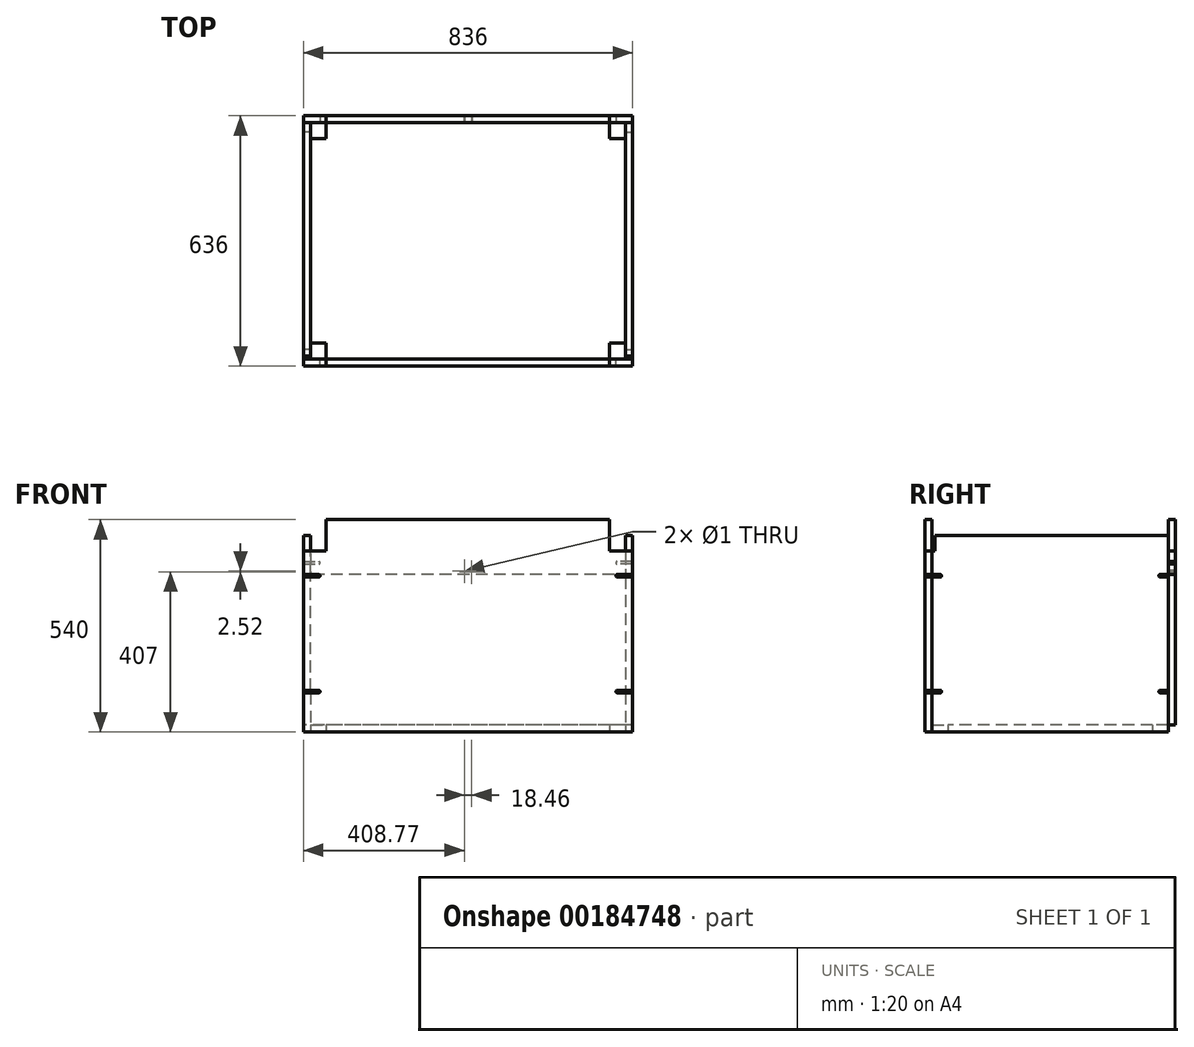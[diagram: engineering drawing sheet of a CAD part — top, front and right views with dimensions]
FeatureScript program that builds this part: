
annotation { "Feature Type Name" : "Feature", "Feature Type Description" : "" }
export const myFeature = defineFeature(function(context is Context, id is Id, definition is map)
    precondition{}
    {
        {
            var Q0;
            Q0=qCreatedBy(makeId("Front.planeOp"),FACE);
            var sketch = newSketch(context, id + "F0", { "sketchPlane" : qUnion([Q0])});
            skLineSegment(sketch, "E0.bottom", {"start": v(418, -250) * mm, "end": v(-418, -250) * mm});
            skLineSegment(sketch, "E0.top", {"start": v(418, 250) * mm, "end": v(-418, 250) * mm});
            skLineSegment(sketch, "E0.left", {"start": v(418, -250) * mm, "end": v(418, 250) * mm});
            skLineSegment(sketch, "E0.right", {"start": v(-418, -250) * mm, "end": v(-418, 250) * mm});
            skPoint(sketch, "E0.middle", {"position": v(0, 0) * mm});
            skLineSegment(sketch, "E1.bottom", {"start": v(-418, 150) * mm, "end": v(-378.8, 150) * mm});
            skLineSegment(sketch, "E1.top", {"start": v(-418, 144) * mm, "end": v(-378.8, 144) * mm});
            skLineSegment(sketch, "E1.left", {"start": v(-418, 150) * mm, "end": v(-418, 144) * mm});
            skLineSegment(sketch, "E1.right", {"start": v(-378.8, 150) * mm, "end": v(-378.8, 144) * mm, "construction": true});
            skArc(sketch, "E2", {"start": v(-378.8, 144) * mm, "mid": v(-375.8, 147) * mm, "end": v(-378.8, 150) * mm});
            skLineSegment(sketch, "E3.MirrorCS", {"start": v(418, 150) * mm, "end": v(378.8, 150) * mm});
            skLineSegment(sketch, "E4.MirrorCS", {"start": v(418, 144) * mm, "end": v(378.8, 144) * mm});
            skArc(sketch, "E5.MirrorCS", {"start": v(378.8, 144) * mm, "mid": v(375.8, 147) * mm, "end": v(378.8, 150) * mm});
            skLineSegment(sketch, "E6.MirrorCS", {"start": v(418, 150) * mm, "end": v(418, 144) * mm});
            skLineSegment(sketch, "E7.MirrorCS", {"start": v(-418, -150) * mm, "end": v(-378.8, -150) * mm});
            skArc(sketch, "E8.MirrorCS", {"start": v(-378.8, -144) * mm, "mid": v(-375.8, -147) * mm, "end": v(-378.8, -150) * mm});
            skLineSegment(sketch, "E9.MirrorCS", {"start": v(-418, -144) * mm, "end": v(-378.8, -144) * mm});
            skLineSegment(sketch, "E10.MirrorCS", {"start": v(-418, -150) * mm, "end": v(-418, -144) * mm});
            skLineSegment(sketch, "E11.MirrorCS", {"start": v(418, -150) * mm, "end": v(378.8, -150) * mm});
            skLineSegment(sketch, "E12.MirrorCS", {"start": v(418, -144) * mm, "end": v(378.8, -144) * mm});
            skArc(sketch, "E13.MirrorCS", {"start": v(378.8, -144) * mm, "mid": v(375.8, -147) * mm, "end": v(378.8, -150) * mm});
            skLineSegment(sketch, "E14.MirrorCS", {"start": v(418, -150) * mm, "end": v(418, -144) * mm});
            skSolve(sketch);
        }
        {
            var Q0;
            Q0=makeQuery(id+"F0.imprint","IMPRINT",FACE,{"disambiguationData":[TD([[makeQuery(id+"F0.imprint","IMPRINT",EDGE,{"derivedFrom":sQuery(id+"F0.wireOp",EDGE,"E0.bottom")}),-1.0]])]});
            extrude(context, id + "F1", {"entities" : qUnion([Q0]), "depth" : 18 * mm});
        }
        {
            var Q0;
            Q0=makeQuery(id+"F1.opExtrude","SWEPT_FACE",FACE,{"disambiguationData":[OSD([sQuery(id+"F0.wireOp",EDGE,"E0.left")])]});
            var sketch = newSketch(context, id + "F2", { "sketchPlane" : qUnion([Q0])});
            skLineSegment(sketch, "E15.bottom", {"start": v(0, 250) * mm, "end": v(600, 250) * mm});
            skLineSegment(sketch, "E15.top", {"start": v(0, -250) * mm, "end": v(600, -250) * mm});
            skLineSegment(sketch, "E15.left", {"start": v(0, 250) * mm, "end": v(0, -250) * mm});
            skLineSegment(sketch, "E15.right", {"start": v(600, 250) * mm, "end": v(600, -250) * mm});
            skLineSegment(sketch, "E16.bottom", {"start": v(0, 150) * mm, "end": v(21.2, 150) * mm});
            skLineSegment(sketch, "E16.top", {"start": v(0, 144) * mm, "end": v(21.2, 144) * mm});
            skLineSegment(sketch, "E16.left", {"start": v(0, 150) * mm, "end": v(0, 144) * mm});
            skLineSegment(sketch, "E16.right", {"start": v(21.2, 150) * mm, "end": v(21.2, 144) * mm, "construction": true});
            skArc(sketch, "E17", {"start": v(21.2, 144) * mm, "mid": v(24.2, 147) * mm, "end": v(21.2, 150) * mm});
            skLineSegment(sketch, "E18.MirrorCS", {"start": v(0, -150) * mm, "end": v(21.2, -150) * mm});
            skLineSegment(sketch, "E19.MirrorCS", {"start": v(0, -144) * mm, "end": v(21.2, -144) * mm});
            skArc(sketch, "E20.MirrorCS", {"start": v(21.2, -144) * mm, "mid": v(24.2, -147) * mm, "end": v(21.2, -150) * mm});
            skLineSegment(sketch, "E21.MirrorCS", {"start": v(0, -150) * mm, "end": v(0, -144) * mm});
            skLineSegment(sketch, "E22", {"start": v(300, 250) * mm, "end": v(300, 116.64) * mm, "construction": true});
            skLineSegment(sketch, "E23.MirrorCS", {"start": v(600, 150) * mm, "end": v(578.8, 150) * mm});
            skLineSegment(sketch, "E24.MirrorCS", {"start": v(600, 144) * mm, "end": v(578.8, 144) * mm});
            skArc(sketch, "E25.MirrorCS", {"start": v(578.8, 144) * mm, "mid": v(575.8, 147) * mm, "end": v(578.8, 150) * mm});
            skLineSegment(sketch, "E26.MirrorCS", {"start": v(600, 150) * mm, "end": v(600, 144) * mm});
            skLineSegment(sketch, "E27.MirrorCS", {"start": v(600, -144) * mm, "end": v(578.8, -144) * mm});
            skLineSegment(sketch, "E28.MirrorCS", {"start": v(600, -150) * mm, "end": v(578.8, -150) * mm});
            skArc(sketch, "E29.MirrorCS", {"start": v(578.8, -144) * mm, "mid": v(575.8, -147) * mm, "end": v(578.8, -150) * mm});
            skSolve(sketch);
        }
        {
            var Q0;
            Q0=makeQuery(id+"F2.imprint","IMPRINT",FACE,{"disambiguationData":[TD([[makeQuery(id+"F2.imprint","IMPRINT",EDGE,{"derivedFrom":sQuery(id+"F2.wireOp",EDGE,"E15.bottom")}),-1.0]])]});
            extrude(context, id + "F3", {"entities" : qUnion([Q0]), "oppositeDirection" : true, "depth" : 18 * mm});
        }
        {
            var Q0;
            {var subQ0=sQuery(id+"F0.wireOp",EDGE,"E0.right");Q0=makeQuery(id+"F1.opExtrude","SWEPT_FACE",FACE,{"disambiguationData":[OSD([subQ0]),TDD([makeQuery(id+"F0.imprint","IMPRINT",EDGE,{"disambiguationData":[TD([[makeQuery(id+"F0.imprint","INTERSECT",VERTEX,{"derivedFrom":[subQ0,sQuery(id+"F0.wireOp",EDGE,"E1.top"),sQuery(id+"F0.wireOp",EDGE,"E1.left")]}),1.0]])],"derivedFrom":subQ0})])]});}
            var sketch = newSketch(context, id + "F4", { "sketchPlane" : qUnion([Q0])});
            skLineSegment(sketch, "E30.0.0", {"start": v(0, 250) * mm, "end": v(-600, 250) * mm});
            skLineSegment(sketch, "E30.0.1", {"start": v(-600, 250) * mm, "end": v(-600, 150) * mm});
            skLineSegment(sketch, "E30.0.2", {"start": v(-600, 150) * mm, "end": v(-578.8, 150) * mm});
            skArc(sketch, "E30.0.3", {"start": v(-578.8, 150) * mm, "mid": v(-575.8, 147) * mm, "end": v(-578.8, 144) * mm});
            skLineSegment(sketch, "E30.0.4", {"start": v(-578.8, 144) * mm, "end": v(-600, 144) * mm});
            skLineSegment(sketch, "E30.0.5", {"start": v(-600, 144) * mm, "end": v(-600, -144) * mm});
            skLineSegment(sketch, "E30.0.6", {"start": v(-600, -144) * mm, "end": v(-578.8, -144) * mm});
            skArc(sketch, "E30.0.7", {"start": v(-578.8, -144) * mm, "mid": v(-575.8, -147) * mm, "end": v(-578.8, -150) * mm});
            skLineSegment(sketch, "E30.0.8", {"start": v(-578.8, -150) * mm, "end": v(-600, -150) * mm});
            skLineSegment(sketch, "E30.0.9", {"start": v(-600, -150) * mm, "end": v(-600, -250) * mm});
            skLineSegment(sketch, "E30.0.10", {"start": v(-600, -250) * mm, "end": v(0, -250) * mm});
            skLineSegment(sketch, "E30.0.11", {"start": v(0, -250) * mm, "end": v(0, -150) * mm});
            skLineSegment(sketch, "E30.0.12", {"start": v(0, -150) * mm, "end": v(-21.2, -150) * mm});
            skArc(sketch, "E30.0.13", {"start": v(-21.2, -150) * mm, "mid": v(-24.2, -147) * mm, "end": v(-21.2, -144) * mm});
            skLineSegment(sketch, "E30.0.14", {"start": v(-21.2, -144) * mm, "end": v(0, -144) * mm});
            skLineSegment(sketch, "E30.0.15", {"start": v(0, -144) * mm, "end": v(0, 144) * mm});
            skLineSegment(sketch, "E30.0.16", {"start": v(0, 144) * mm, "end": v(-21.2, 144) * mm});
            skArc(sketch, "E30.0.17", {"start": v(-21.2, 144) * mm, "mid": v(-24.2, 147) * mm, "end": v(-21.2, 150) * mm});
            skLineSegment(sketch, "E30.0.18", {"start": v(-21.2, 150) * mm, "end": v(0, 150) * mm});
            skLineSegment(sketch, "E30.0.19", {"start": v(0, 150) * mm, "end": v(0, 250) * mm});
            skSolve(sketch);
        }
        {
            var Q0;
            Q0=makeQuery(id+"F4.imprint","IMPRINT",FACE,{"disambiguationData":[TD([[makeQuery(id+"F4.imprint","IMPRINT",EDGE,{"derivedFrom":sQuery(id+"F4.wireOp",EDGE,"E30.0.0")}),1.0]])]});
            extrude(context, id + "F5", {"entities" : qUnion([Q0]), "oppositeDirection" : true, "depth" : 18 * mm});
        }
        {
            var Q0;
            Q0=makeQuery(id+"F1.opExtrude","CAP_FACE",FACE,{"disambiguationData":[OSD([sQuery(id+"F0.wireOp",EDGE,"E0.bottom"),sQuery(id+"F0.wireOp",EDGE,"E0.top"),sQuery(id+"F0.wireOp",EDGE,"E0.left"),sQuery(id+"F0.wireOp",EDGE,"E0.right"),sQuery(id+"F0.wireOp",EDGE,"E1.bottom"),sQuery(id+"F0.wireOp",EDGE,"E1.top"),sQuery(id+"F0.wireOp",EDGE,"E2"),sQuery(id+"F0.wireOp",EDGE,"E3.MirrorCS"),sQuery(id+"F0.wireOp",EDGE,"E4.MirrorCS"),sQuery(id+"F0.wireOp",EDGE,"E5.MirrorCS"),sQuery(id+"F0.wireOp",EDGE,"E7.MirrorCS"),sQuery(id+"F0.wireOp",EDGE,"E8.MirrorCS"),sQuery(id+"F0.wireOp",EDGE,"E9.MirrorCS"),sQuery(id+"F0.wireOp",EDGE,"E11.MirrorCS"),sQuery(id+"F0.wireOp",EDGE,"E12.MirrorCS"),sQuery(id+"F0.wireOp",EDGE,"E13.MirrorCS")])],"isStart":false});
            var sketch = newSketch(context, id + "F6", { "sketchPlane" : qUnion([Q0])});
            skLineSegment(sketch, "E31.bottom", {"start": v(-418, 250) * mm, "end": v(-360, 250) * mm});
            skLineSegment(sketch, "E31.top", {"start": v(-418, 210) * mm, "end": v(-360, 210) * mm});
            skLineSegment(sketch, "E31.left", {"start": v(-418, 250) * mm, "end": v(-418, 210) * mm});
            skLineSegment(sketch, "E31.right", {"start": v(-360, 250) * mm, "end": v(-360, 210) * mm});
            skLineSegment(sketch, "E32.MirrorCS", {"start": v(418, 210) * mm, "end": v(360, 210) * mm});
            skLineSegment(sketch, "E33.MirrorCS", {"start": v(418, 250) * mm, "end": v(418, 210) * mm});
            skLineSegment(sketch, "E34.MirrorCS", {"start": v(360, 250) * mm, "end": v(360, 210) * mm});
            skLineSegment(sketch, "E35.MirrorCS", {"start": v(418, 250) * mm, "end": v(360, 250) * mm});
            skSolve(sketch);
        }
        {
            var Q0;
            Q0=makeQuery(id+"F6.imprint","IMPRINT",FACE,{"disambiguationData":[TD([[makeQuery(id+"F6.imprint","IMPRINT",EDGE,{"derivedFrom":sQuery(id+"F6.wireOp",EDGE,"E31.bottom")}),1.0]])]});
            var Q1;
            Q1=makeQuery(id+"F6.imprint","IMPRINT",FACE,{"disambiguationData":[TD([[makeQuery(id+"F6.imprint","IMPRINT",EDGE,{"derivedFrom":sQuery(id+"F6.wireOp",EDGE,"E32.MirrorCS")}),-1.0]])]});
            extrude(context, id + "F7", {"entities" : qUnion([Q0, Q1]), "operationType" : NewBodyOperationType.REMOVE, "oppositeDirection" : true, "depth" : 25 * mm});
        }
        {
            var Q0;
            Q0=makeQuery(id+"F1.opExtrude","SWEPT_FACE",FACE,{"disambiguationData":[OSD([sQuery(id+"F0.wireOp",EDGE,"E0.top")])]});
            extrude(context, id + "F8", {"entities" : qUnion([Q0]), "operationType" : NewBodyOperationType.ADD, "depth" : 40 * mm});
        }
        {
            var Q0;
            Q0=makeQuery(id+"F1.opExtrude","SWEPT_FACE",FACE,{"disambiguationData":[OSD([sQuery(id+"F0.wireOp",EDGE,"E0.bottom")])]});
            var sketch = newSketch(context, id + "F9", { "sketchPlane" : qUnion([Q0])});
            skLineSegment(sketch, "E36.0", {"start": v(-400, -600) * mm, "end": v(-400, 0) * mm});
            skLineSegment(sketch, "E37.0", {"start": v(400, 0) * mm, "end": v(400, -600) * mm});
            skLineSegment(sketch, "E38", {"start": v(-400, 0) * mm, "end": v(400, 0) * mm});
            skLineSegment(sketch, "E39", {"start": v(400, -600) * mm, "end": v(-400, -600) * mm});
            skLineSegment(sketch, "E40.bottom", {"start": v(400, -600) * mm, "end": v(360, -600) * mm});
            skLineSegment(sketch, "E40.top", {"start": v(400, -560) * mm, "end": v(360, -560) * mm});
            skLineSegment(sketch, "E40.left", {"start": v(400, -600) * mm, "end": v(400, -560) * mm});
            skLineSegment(sketch, "E40.right", {"start": v(360, -600) * mm, "end": v(360, -560) * mm});
            skLineSegment(sketch, "E41.MirrorCS", {"start": v(-360, -600) * mm, "end": v(-360, -560) * mm});
            skLineSegment(sketch, "E42.MirrorCS", {"start": v(-400, -560) * mm, "end": v(-360, -560) * mm});
            skLineSegment(sketch, "E43", {"start": v(400, -300) * mm, "end": v(241.27, -300) * mm, "construction": true});
            skLineSegment(sketch, "E44.MirrorCS", {"start": v(400, -40) * mm, "end": v(360, -40) * mm});
            skLineSegment(sketch, "E45.MirrorCS", {"start": v(360, 0) * mm, "end": v(360, -40) * mm});
            skLineSegment(sketch, "E46.MirrorCS", {"start": v(-400, -40) * mm, "end": v(-360, -40) * mm});
            skLineSegment(sketch, "E47.MirrorCS", {"start": v(-360, 0) * mm, "end": v(-360, -40) * mm});
            skSolve(sketch);
        }
        {
            var Q0;
            {var subQ6=sQuery(id+"F9.wireOp",EDGE,"E40.top");Q0=makeQuery(id+"F9.imprint","IMPRINT",FACE,{"disambiguationData":[TD([[makeQuery(id+"F9.imprint","IMPRINT",EDGE,{"derivedFrom":subQ6}),-1.0]])]});}
            extrude(context, id + "F10", {"entities" : qUnion([Q0]), "oppositeDirection" : true, "depth" : 18 * mm});
        }
        {
            var Q0;
            {var subQ0=sQuery(id+"F2.wireOp",EDGE,"E15.right");Q0=makeQuery(id+"F3.opExtrude","SWEPT_FACE",FACE,{"disambiguationData":[OSD([subQ0]),TDD([makeQuery(id+"F2.imprint","IMPRINT",EDGE,{"disambiguationData":[TD([[makeQuery(id+"F2.imprint","INTERSECT",VERTEX,{"derivedFrom":[subQ0,sQuery(id+"F2.wireOp",EDGE,"E27.MirrorCS")]}),1.0]])],"derivedFrom":subQ0})])]});}
            var sketch = newSketch(context, id + "F11", { "sketchPlane" : qUnion([Q0])});
            skLineSegment(sketch, "E48.0", {"start": v(-360, 290) * mm, "end": v(360, 290) * mm});
            skLineSegment(sketch, "E49.0", {"start": v(-360, 290) * mm, "end": v(-360, 210) * mm});
            skLineSegment(sketch, "E50.0", {"start": v(360, 290) * mm, "end": v(360, 210) * mm});
            skLineSegment(sketch, "E51.0", {"start": v(418, 210) * mm, "end": v(360, 210) * mm});
            skLineSegment(sketch, "E52.0", {"start": v(-418, 210) * mm, "end": v(-360, 210) * mm});
            skLineSegment(sketch, "E53.0", {"start": v(-418, 150) * mm, "end": v(-418, 210) * mm});
            skLineSegment(sketch, "E54.0", {"start": v(418, 150) * mm, "end": v(418, 210) * mm});
            skLineSegment(sketch, "E55", {"start": v(-418, 150) * mm, "end": v(418, 150) * mm});
            skLineSegment(sketch, "E56.0", {"start": v(-360, -232) * mm, "end": v(360, -232) * mm, "construction": true});
            skLineSegment(sketch, "E57.0", {"start": v(418, -144) * mm, "end": v(418, 144) * mm, "construction": true});
            skLineSegment(sketch, "E58.top", {"start": v(-418, -232) * mm, "end": v(418, -232) * mm});
            skLineSegment(sketch, "E58.left", {"start": v(-418, 150) * mm, "end": v(-418, -232) * mm});
            skLineSegment(sketch, "E58.right", {"start": v(418, 150) * mm, "end": v(418, -232) * mm});
            skCircle(sketch, "E59", {"center": v(-378.8, 180) * mm, "radius": 3 * mm, "construction": true});
            skPoint(sketch, "E59.centerSnap0", {"position": v(-418, 180) * mm});
            skLineSegment(sketch, "E60.bottom", {"start": v(-418, 183) * mm, "end": v(-378.8, 183) * mm});
            skLineSegment(sketch, "E60.top", {"start": v(-418, 177) * mm, "end": v(-378.8, 177) * mm});
            skLineSegment(sketch, "E60.left", {"start": v(-418, 183) * mm, "end": v(-418, 177) * mm});
            skArc(sketch, "E61", {"start": v(-378.8, 177) * mm, "mid": v(-375.8, 180) * mm, "end": v(-378.8, 183) * mm});
            skLineSegment(sketch, "E62.MirrorCS", {"start": v(418, 183) * mm, "end": v(378.8, 183) * mm});
            skLineSegment(sketch, "E63.MirrorCS", {"start": v(418, 177) * mm, "end": v(378.8, 177) * mm});
            skCircle(sketch, "E64.MirrorC", {"center": v(378.8, 180) * mm, "radius": 3 * mm, "construction": true});
            skLineSegment(sketch, "E65.MirrorCS", {"start": v(418, 183) * mm, "end": v(418, 177) * mm});
            skArc(sketch, "E66.MirrorCS", {"start": v(378.8, 177) * mm, "mid": v(375.8, 180) * mm, "end": v(378.8, 183) * mm});
            skPoint(sketch, "E67.MirrorP", {"position": v(418, 180) * mm});
            skLineSegment(sketch, "E68.bottom", {"start": v(16.23, 150) * mm, "end": v(-16.23, 150) * mm});
            skLineSegment(sketch, "E68.top", {"start": v(16.23, 165.52) * mm, "end": v(-16.23, 165.52) * mm, "construction": true});
            skLineSegment(sketch, "E68.left", {"start": v(16.23, 150) * mm, "end": v(16.23, 165.52) * mm, "construction": true});
            skLineSegment(sketch, "E68.right", {"start": v(-16.23, 150) * mm, "end": v(-16.23, 165.52) * mm, "construction": true});
            skPoint(sketch, "E68.middle", {"position": v(0, 157.76) * mm});
            skPoint(sketch, "E68.middle.positionSnap0", {"position": v(0, 290) * mm});
            skPoint(sketch, "E68.centerSnap0", {"position": v(0, 290) * mm});
            skCircle(sketch, "E69", {"center": v(-9.23, 157) * mm, "radius": 0.5 * mm});
            skCircle(sketch, "E70", {"center": v(9.23, 159.52) * mm, "radius": 0.5 * mm});
            skSolve(sketch);
        }
        {
            var Q0;
            Q0=makeQuery(id+"F11.imprint","IMPRINT",FACE,{"disambiguationData":[TD([[makeQuery(id+"F11.imprint","IMPRINT",EDGE,{"derivedFrom":sQuery(id+"F11.wireOp",EDGE,"E48.0")}),-1.0]])]});
            extrude(context, id + "F12", {"entities" : qUnion([Q0]), "depth" : 18 * mm});
        }
        {
            var Q0;
            {var subQ3=sQuery(id+"F2.wireOp",EDGE,"E15.right");var subQ5=sQuery(id+"F2.wireOp",EDGE,"E27.MirrorCS");var subQ6=makeQuery(id+"F3.opExtrude","SWEPT_EDGE",EDGE,{"disambiguationData":[OSD([subQ3,subQ5])]});Q0=makeQuery(id+"F11.imprint","IMPRINT",FACE,{"disambiguationData":[TD([[makeQuery(id+"F11.imprint","IMPRINT",EDGE,{"derivedFrom":subQ6}),-1.0]])]});}
            var Q1;
            {var subQ8=sQuery(id+"F11.wireOp",EDGE,"E55");Q1=makeQuery(id+"F11.imprint","IMPRINT",FACE,{"disambiguationData":[TD([[makeQuery(id+"F11.imprint","IMPRINT",EDGE,{"derivedFrom":subQ8}),-1.0]])]});}
            extrude(context, id + "F13", {"entities" : qUnion([Q0, Q1]), "depth" : 18 * mm});
        }
    });
